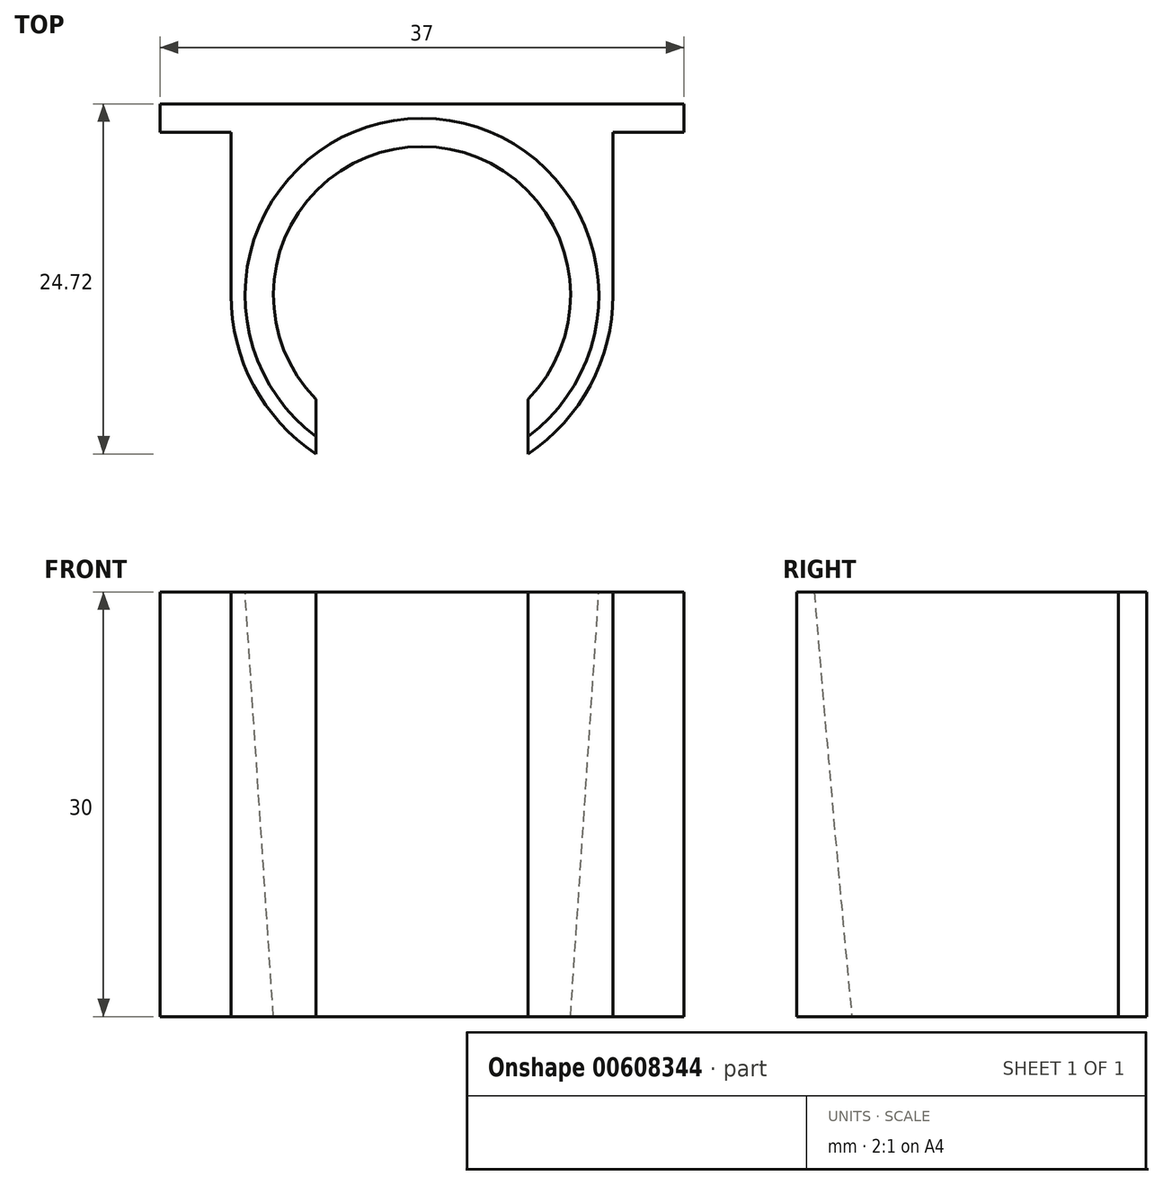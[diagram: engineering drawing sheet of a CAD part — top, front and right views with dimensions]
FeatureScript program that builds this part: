
annotation { "Feature Type Name" : "Feature", "Feature Type Description" : "" }
export const myFeature = defineFeature(function(context is Context, id is Id, definition is map)
    precondition{}
    {
        {
            var Q0;
            Q0=qCreatedBy(makeId("Top.planeOp"),FACE);
            var sketch = newSketch(context, id + "F0", { "sketchPlane" : qUnion([Q0])});
            skLineSegment(sketch, "E0", {"start": v(13.5, 11.5) * mm, "end": v(18.5, 11.5) * mm});
            skLineSegment(sketch, "E1", {"start": v(18.5, 11.5) * mm, "end": v(18.5, 13.5) * mm});
            skLineSegment(sketch, "E2", {"start": v(18.5, 13.5) * mm, "end": v(-18.5, 13.5) * mm});
            skLineSegment(sketch, "E3", {"start": v(-18.5, 13.5) * mm, "end": v(-18.5, 11.5) * mm});
            skLineSegment(sketch, "E4", {"start": v(-18.5, 11.5) * mm, "end": v(-13.5, 11.5) * mm});
            skLineSegment(sketch, "E5.top", {"start": v(-13.5, 13.5) * mm, "end": v(13.5, 13.5) * mm});
            skLineSegment(sketch, "E5.left", {"start": v(-13.5, 0) * mm, "end": v(-13.5, 11.5) * mm});
            skLineSegment(sketch, "E5.right", {"start": v(13.5, 0) * mm, "end": v(13.5, 11.5) * mm});
            skCircle(sketch, "E6", {"center": v(0, 0) * mm, "radius": 13.5 * mm});
            skCircle(sketch, "E7", {"center": v(0, 0) * mm, "radius": 10.5 * mm});
            skLineSegment(sketch, "E8", {"start": v(-13.5, 0) * mm, "end": v(13.5, 0) * mm, "construction": true});
            skLineSegment(sketch, "E9.bottom", {"start": v(-7.5, 0) * mm, "end": v(7.5, 0) * mm});
            skLineSegment(sketch, "E9.top", {"start": v(-7.5, -16.3) * mm, "end": v(7.5, -16.3) * mm});
            skLineSegment(sketch, "E9.left", {"start": v(-7.5, 0) * mm, "end": v(-7.5, -16.3) * mm});
            skLineSegment(sketch, "E9.right", {"start": v(7.5, 0) * mm, "end": v(7.5, -16.3) * mm});
            skSolve(sketch);
        }
        {
            var Q0;
            {var subQ5=sQuery(id+"F0.wireOp",EDGE,"E3");Q0=makeQuery(id+"F0.imprint","IMPRINT",FACE,{"disambiguationData":[TD([[makeQuery(id+"F0.imprint","IMPRINT",EDGE,{"derivedFrom":subQ5}),1.0]])]});}
            var Q1;
            Q1=makeQuery(id+"F0.imprint","IMPRINT",FACE,{"disambiguationData":[TD([[makeQuery(id+"F0.imprint","IMPRINT",EDGE,{"derivedFrom":sQuery(id+"F0.wireOp",EDGE,"E0")}),1.0]])]});
            var Q2;
            {var subQ0=sQuery(id+"F0.wireOp",EDGE,"E6");var subQ1=makeQuery(id+"F0.imprint","INTERSECT",VERTEX,{"derivedFrom":[sQuery(id+"F0.wireOp",EDGE,"E5.right"),subQ0]});Q2=makeQuery(id+"F0.imprint","IMPRINT",FACE,{"disambiguationData":[TD([[makeQuery(id+"F0.imprint","IMPRINT",EDGE,{"disambiguationData":[TD([[subQ1,-1.0]])],"derivedFrom":subQ0}),1.0]])]});}
            extrude(context, id + "F1", {"entities" : qUnion([Q0, Q1, Q2]), "depth" : 30 * mm, "offsetDistance" : 25 * mm});
        }
        {
            var Q0;
            Q0=qCreatedBy(makeId("Front.planeOp"),FACE);
            var sketch = newSketch(context, id + "F2", { "sketchPlane" : qUnion([Q0])});
            skLineSegment(sketch, "E10", {"start": v(10.5, 0) * mm, "end": v(12.5, 30) * mm});
            skLineSegment(sketch, "E11", {"start": v(12.5, 30) * mm, "end": v(0, 30) * mm, "construction": true});
            skLineSegment(sketch, "E12", {"start": v(10.5, 0) * mm, "end": v(0, 0) * mm, "construction": true});
            skLineSegment(sketch, "E13", {"start": v(0, 0) * mm, "end": v(0, 30) * mm});
            skLineSegment(sketch, "E14", {"start": v(10.5, 0) * mm, "end": v(0, 0) * mm});
            skLineSegment(sketch, "E15", {"start": v(12.5, 30) * mm, "end": v(0, 30) * mm});
            skSolve(sketch);
        }
        {
            var Q0;
            Q0 = qSketchRegion(id + "F2", true);
            var Q1;
            Q1=sQuery(id+"F2.wireOp",EDGE,"E13");
            revolve(context, id + "F3", {"operationType" : NewBodyOperationType.REMOVE, "surfaceOperationType" : NewSurfaceOperationType.NEW, "entities" : qUnion([Q0]), "axis" : qUnion([Q1]), "revolveType" : RevolveType.FULL});
        }
    });
